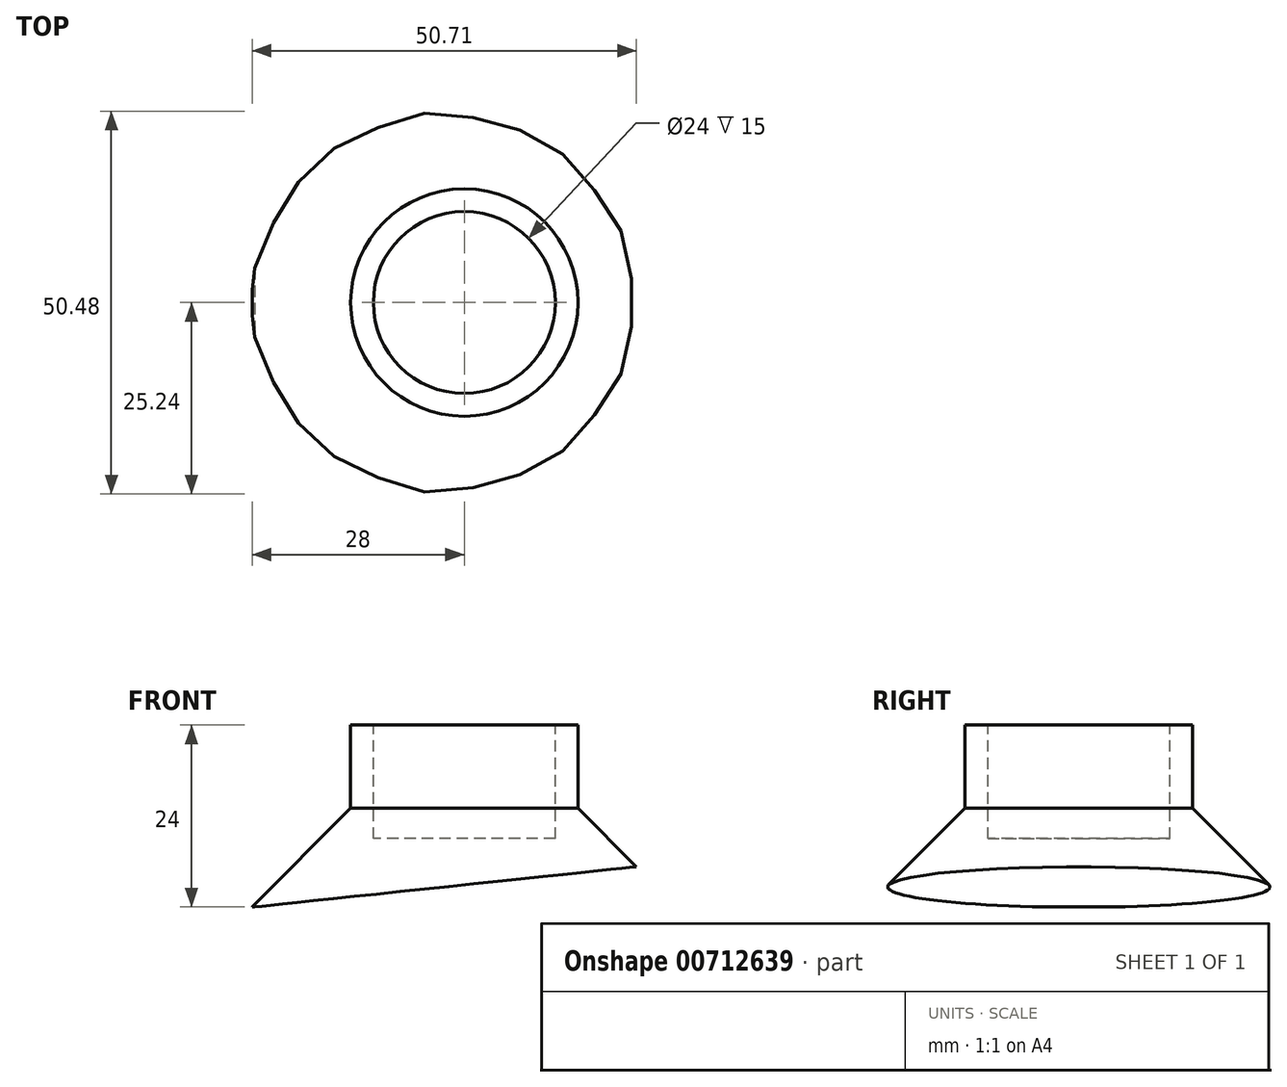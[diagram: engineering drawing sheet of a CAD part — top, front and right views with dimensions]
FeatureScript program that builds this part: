
annotation { "Feature Type Name" : "Feature", "Feature Type Description" : "" }
export const myFeature = defineFeature(function(context is Context, id is Id, definition is map)
    precondition{}
    {
        {
            var Q0;
            Q0=qCreatedBy(makeId("Front.planeOp"),FACE);
            var sketch = newSketch(context, id + "F0", { "sketchPlane" : qUnion([Q0])});
            skLineSegment(sketch, "E0", {"start": v(0, 0) * mm, "end": v(28, 0) * mm});
            skLineSegment(sketch, "E1", {"start": v(28, 0) * mm, "end": v(15, 13) * mm});
            skLineSegment(sketch, "E2", {"start": v(15, 13) * mm, "end": v(15, 24) * mm});
            skLineSegment(sketch, "E3", {"start": v(15, 24) * mm, "end": v(0, 24) * mm});
            skLineSegment(sketch, "E4", {"start": v(0, 24) * mm, "end": v(0, 0) * mm});
            skSolve(sketch);
        }
        {
            var Q0;
            Q0 = qSketchRegion(id + "F0", true);
            var Q1;
            Q1=sQuery(id+"F0.wireOp",EDGE,"E4");
            revolve(context, id + "F1", {"surfaceOperationType" : NewSurfaceOperationType.NEW, "entities" : qUnion([Q0]), "axis" : qUnion([Q1]), "revolveType" : RevolveType.FULL});
        }
        {
            var Q0;
            Q0=makeQuery(id+"F1.opRevolve","SWEPT_FACE",FACE,{"disambiguationData":[OSD([sQuery(id+"F0.wireOp",EDGE,"E3")])]});
            var sketch = newSketch(context, id + "F2", { "sketchPlane" : qUnion([Q0])});
            skCircle(sketch, "E5", {"center": v(0, 0) * mm, "radius": 12 * mm});
            skSolve(sketch);
        }
        {
            var Q0;
            Q0 = qSketchRegion(id + "F2", true);
            extrude(context, id + "F3", {"entities" : qUnion([Q0]), "operationType" : NewBodyOperationType.REMOVE, "oppositeDirection" : true, "depth" : 15 * mm, "offsetDistance" : 25 * mm});
        }
        {
            var Q0;
            Q0=qCreatedBy(makeId("Front.planeOp"),FACE);
            var sketch = newSketch(context, id + "F4", { "sketchPlane" : qUnion([Q0])});
            skLineSegment(sketch, "E6", {"start": v(-27.63, 0) * mm, "end": v(33.36, 6.41) * mm});
            skLineSegment(sketch, "E7", {"start": v(33.36, 6.41) * mm, "end": v(33.36, 0) * mm});
            skLineSegment(sketch, "E8", {"start": v(33.36, 0) * mm, "end": v(-27.63, 0) * mm});
            skSolve(sketch);
        }
        {
            var Q0;
            Q0 = qSketchRegion(id + "F4", true);
            extrude(context, id + "F5", {"entities" : qUnion([Q0]), "operationType" : NewBodyOperationType.REMOVE, "endBound" : BoundingType.SYMMETRIC, "oppositeDirection" : true, "depth" : 100 * mm, "offsetDistance" : 25 * mm});
        }
    });
